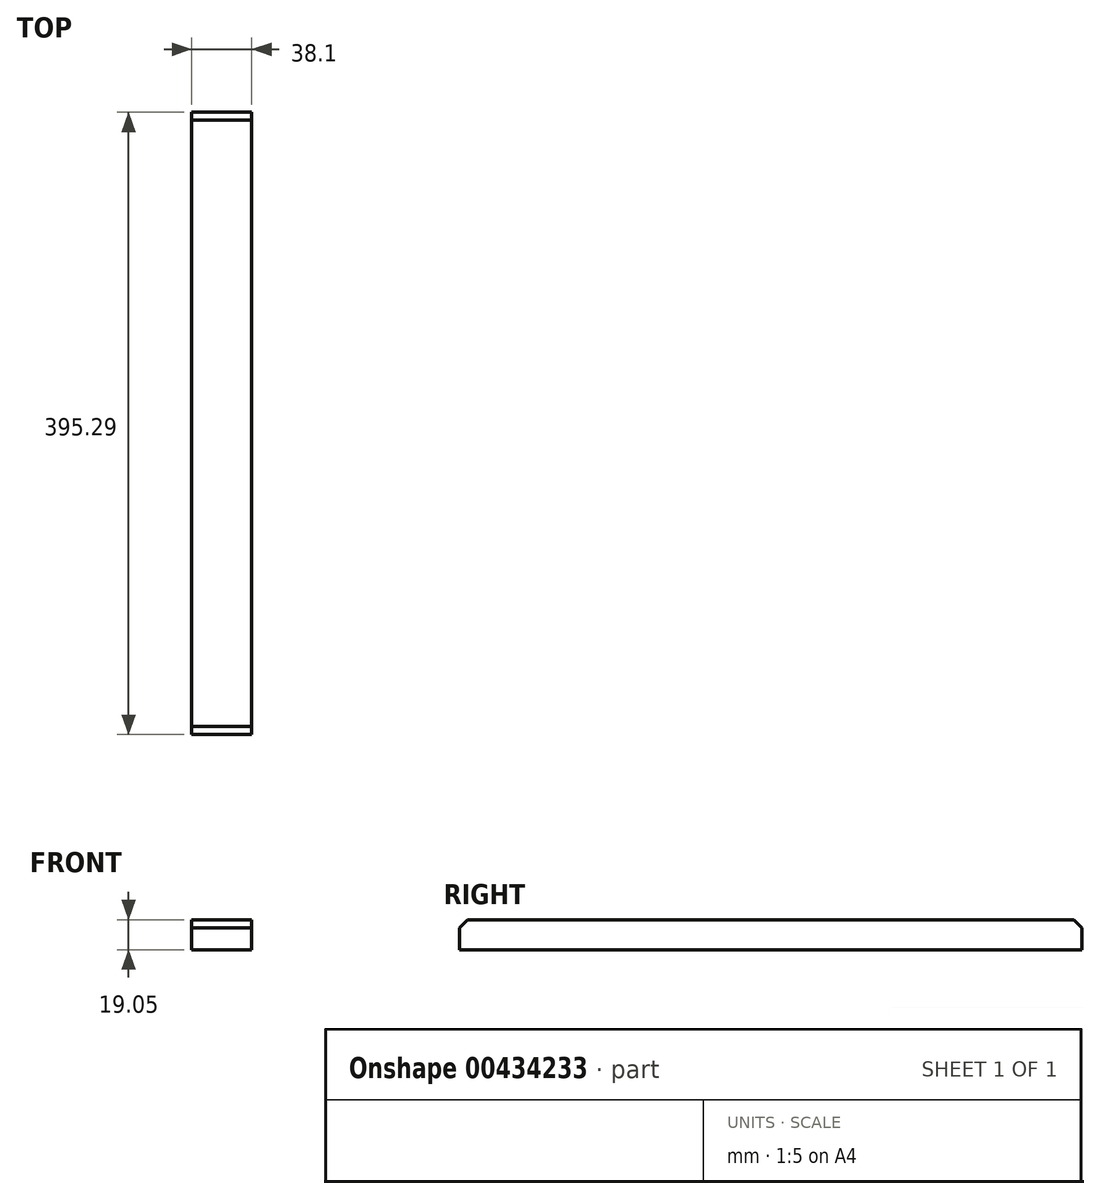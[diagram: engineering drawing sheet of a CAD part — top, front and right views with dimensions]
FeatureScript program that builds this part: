
annotation { "Feature Type Name" : "Feature", "Feature Type Description" : "" }
export const myFeature = defineFeature(function(context is Context, id is Id, definition is map)
    precondition{}
    {
        {
            var Q0;
            Q0=qCreatedBy(makeId("Front.planeOp"),FACE);
            var sketch = newSketch(context, id + "F0", { "sketchPlane" : qUnion([Q0])});
            skLineSegment(sketch, "E0.bottom", {"start": v(0, 0) * mm, "end": v(38.1, 0) * mm});
            skLineSegment(sketch, "E0.top", {"start": v(0, 19.05) * mm, "end": v(38.1, 19.05) * mm});
            skLineSegment(sketch, "E0.left", {"start": v(0, 0) * mm, "end": v(0, 19.05) * mm});
            skLineSegment(sketch, "E0.right", {"start": v(38.1, 0) * mm, "end": v(38.1, 19.05) * mm});
            skSolve(sketch);
        }
        {
            var Q0;
            Q0 = qSketchRegion(id + "F0", true);
            extrude(context, id + "F1", {"entities" : qUnion([Q0]), "depth" : 395.3 * mm});
        }
        {
            var Q0;
            Q0=makeQuery(id+"F1.opExtrude","CAP_EDGE",EDGE,{"disambiguationData":[OSD([sQuery(id+"F0.wireOp",EDGE,"E0.top")])],"isStart":false});
            var Q1;
            Q1=makeQuery(id+"F1.opExtrude","CAP_EDGE",EDGE,{"disambiguationData":[OSD([sQuery(id+"F0.wireOp",EDGE,"E0.top")])],"isStart":true});
            chamfer(context, id + "F2", {"entities" : qUnion([Q0, Q1]), "width" : 5.08 * mm, "tangentPropagation" : true});
        }
    });
